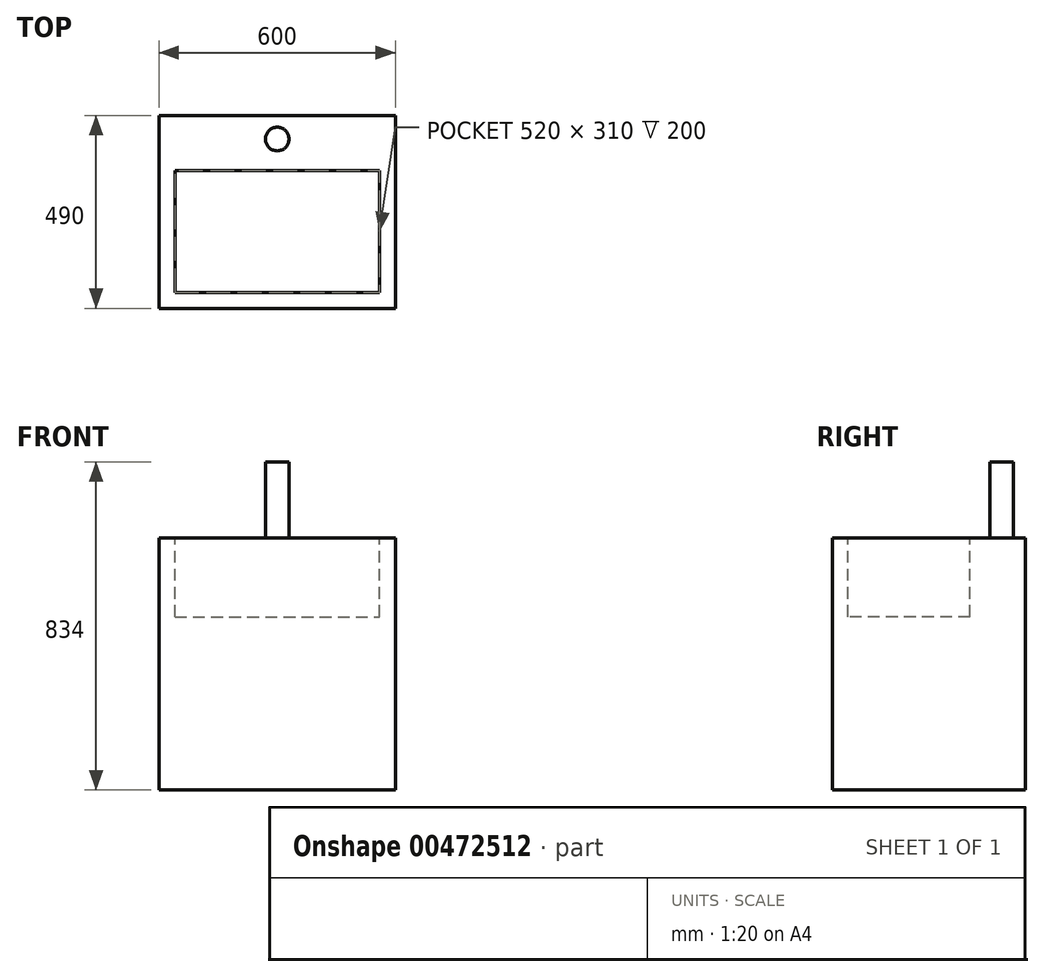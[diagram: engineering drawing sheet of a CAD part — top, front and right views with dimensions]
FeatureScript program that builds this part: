
annotation { "Feature Type Name" : "Feature", "Feature Type Description" : "" }
export const myFeature = defineFeature(function(context is Context, id is Id, definition is map)
    precondition{}
    {
        {
            var Q0;
            Q0=qCreatedBy(makeId("Top.planeOp"),FACE);
            var sketch = newSketch(context, id + "F0", { "sketchPlane" : qUnion([Q0])});
            skLineSegment(sketch, "E0.bottom", {"start": v(-294.1, 316.03) * mm, "end": v(305.9, 316.03) * mm});
            skLineSegment(sketch, "E0.top", {"start": v(-294.1, -173.97) * mm, "end": v(305.9, -173.97) * mm});
            skLineSegment(sketch, "E0.left", {"start": v(-294.1, 316.03) * mm, "end": v(-294.1, -173.97) * mm});
            skLineSegment(sketch, "E0.right", {"start": v(305.9, 316.03) * mm, "end": v(305.9, -173.97) * mm});
            skSolve(sketch);
        }
        {
            var Q0;
            Q0 = qSketchRegion(id + "F0", true);
            extrude(context, id + "F1", {"entities" : qUnion([Q0]), "depth" : 640 * mm, "offsetDistance" : 25 * mm});
        }
        {
            var Q0;
            Q0=makeQuery(id+"F1.opExtrude","CAP_FACE",FACE,{"disambiguationData":[OSD([sQuery(id+"F0.wireOp",EDGE,"E0.bottom"),sQuery(id+"F0.wireOp",EDGE,"E0.top"),sQuery(id+"F0.wireOp",EDGE,"E0.left"),sQuery(id+"F0.wireOp",EDGE,"E0.right")])],"isStart":false});
            var sketch = newSketch(context, id + "F2", { "sketchPlane" : qUnion([Q0])});
            skLineSegment(sketch, "E1.bottom", {"start": v(-254.1, 176.03) * mm, "end": v(265.9, 176.03) * mm});
            skLineSegment(sketch, "E1.top", {"start": v(-254.1, -133.97) * mm, "end": v(265.9, -133.97) * mm});
            skLineSegment(sketch, "E1.left", {"start": v(-254.1, 176.03) * mm, "end": v(-254.1, -133.97) * mm});
            skLineSegment(sketch, "E1.right", {"start": v(265.9, 176.03) * mm, "end": v(265.9, -133.97) * mm});
            skSolve(sketch);
        }
        {
            var Q0;
            Q0=makeQuery(id+"F2.imprint","IMPRINT",FACE,{"disambiguationData":[TD([[makeQuery(id+"F2.imprint","IMPRINT",EDGE,{"derivedFrom":sQuery(id+"F2.wireOp",EDGE,"E1.bottom")}),-1.0]])]});
            extrude(context, id + "F3", {"entities" : qUnion([Q0]), "operationType" : NewBodyOperationType.REMOVE, "oppositeDirection" : true, "depth" : 200 * mm, "offsetDistance" : 25 * mm});
        }
        {
            var Q0;
            Q0=makeQuery(id+"F1.opExtrude","CAP_FACE",FACE,{"disambiguationData":[OSD([sQuery(id+"F0.wireOp",EDGE,"E0.bottom"),sQuery(id+"F0.wireOp",EDGE,"E0.top"),sQuery(id+"F0.wireOp",EDGE,"E0.left"),sQuery(id+"F0.wireOp",EDGE,"E0.right")])],"isStart":false});
            var sketch = newSketch(context, id + "F4", { "sketchPlane" : qUnion([Q0])});
            skLineSegment(sketch, "E2", {"start": v(5.9, 316.03) * mm, "end": v(5.9, 256.03) * mm, "construction": true});
            skCircle(sketch, "E3", {"center": v(5.9, 256.03) * mm, "radius": 30 * mm});
            skSolve(sketch);
        }
        {
            var Q0;
            Q0=makeQuery(id+"F4.imprint","IMPRINT",FACE,{"disambiguationData":[TD([[makeQuery(id+"F4.imprint","IMPRINT",EDGE,{"derivedFrom":sQuery(id+"F4.wireOp",EDGE,"E3")}),1.0]])]});
            extrude(context, id + "F5", {"entities" : qUnion([Q0]), "operationType" : NewBodyOperationType.ADD, "depth" : 194 * mm, "offsetDistance" : 25 * mm});
        }
    });
